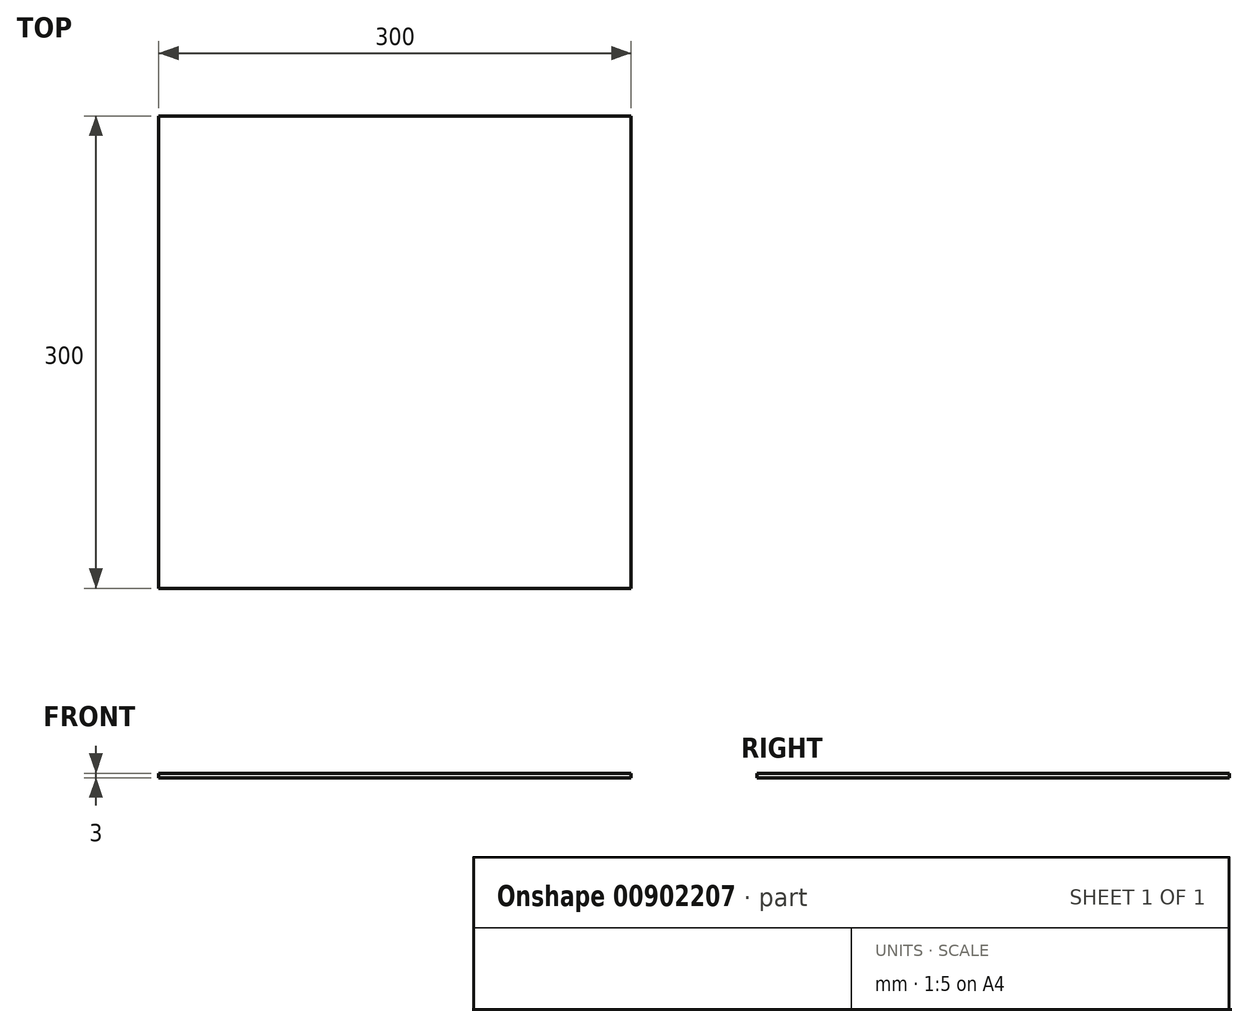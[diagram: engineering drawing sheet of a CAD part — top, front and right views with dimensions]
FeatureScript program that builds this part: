
annotation { "Feature Type Name" : "Feature", "Feature Type Description" : "" }
export const myFeature = defineFeature(function(context is Context, id is Id, definition is map)
    precondition{}
    {
        {
            var Q0;
            Q0=qCreatedBy(makeId("Top.planeOp"),FACE);
            var sketch = newSketch(context, id + "F0", { "sketchPlane" : qUnion([Q0])});
            skLineSegment(sketch, "E0.bottom", {"start": v(0, 0) * mm, "end": v(300, 0) * mm});
            skLineSegment(sketch, "E0.top", {"start": v(0, 300) * mm, "end": v(300, 300) * mm});
            skLineSegment(sketch, "E0.left", {"start": v(0, 0) * mm, "end": v(0, 300) * mm});
            skLineSegment(sketch, "E0.right", {"start": v(300, 0) * mm, "end": v(300, 300) * mm});
            skSolve(sketch);
        }
        {
            var Q0;
            Q0=qSketchRegion(id+"F0",true);
            extrude(context, id + "F1", {"entities" : qUnion([Q0]), "depth" : 3 * mm, "offsetDistance" : 25 * mm});
        }
    });
